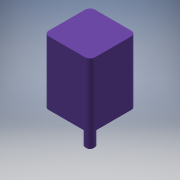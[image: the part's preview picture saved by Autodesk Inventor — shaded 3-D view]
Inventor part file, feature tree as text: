
AUTODESK INVENTOR PART (.ipt)
format: ipt  version: 2016 (Build 200138000, 138)  size: 130,560 bytes
history: native  units: mm
features: reference x5, extrude x3, sketch x3, hole x1, chamfer x1, fillet x1
ambient origin geometry x8: Origin, YZ Plane, XZ Plane, XY Plane, X Axis, Y Axis, Z Axis, Center Point
bodies: Solid1 (feature_tree)
feature tree (14):
  extrude  "Extrusion1"  Depth=20.32mm
  hole  "Hole1"  [1 undecoded]
  sketch  "Sketch3"  dims[d5=3.0mm d6=6.0mm d7=4.0mm d8=2.0mm d9=90.0deg d10=8.0mm d11=20.594885mm d12=1.5mm d13=0.0mm d14=4.0mm d15=15.0mm d16=0.0mm d17=0.6mm d18=2.0mm d19=45.0deg d20=2.16mm]
  extrude  "Extrusion2"  Depth=1.5mm TaperAngle=0.0deg
  extrude  "Extrusion3"  Depth=2.16mm
  chamfer  "Chamfer1"  Distance=15.0mm
  fillet  "Fillet1"  Radius=2.0mm
  sketch  "Sketch1"  dims[d0=20.32mm d1=20.32mm]
  reference  "Reference1"
  reference  "Reference2"
  reference  "Reference3"
  reference  "Reference4"
  reference  "Reference5"
  sketch  "Sketch2"  dims[d2=14.99mm d3=28.0mm d4=0.0mm]
note: 1 required parameter value undecoded (feature->parameter linkage not recoverable at this tier; creation-order binding heuristic only, values carry confidence <= 0.55)
